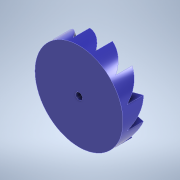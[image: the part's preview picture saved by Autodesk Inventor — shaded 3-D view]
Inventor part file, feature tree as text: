
AUTODESK INVENTOR PART (.ipt)
format: ipt  version: 2021 (Build 250183000, 183)  size: 309,760 bytes
history: native  units: in
note: dims shown in document units (in); Inventor stores cm internally (conversion verified against a paired STEP export)
features: other x3, extrude x2, sketch x2, fillet x1, plane x1
ambient origin geometry x8: Origin, YZ Plane, XZ Plane, XY Plane, X Axis, Y Axis, Z Axis, Center Point
bodies: Solid1 (feature_tree)
feature tree (9):
  other  "mergedprototype.iam"
  other  "prototypeDown.ipt:1"
  other  "cylinder.ipt:1"
  extrude  "Extrusion1"  Depth=0.3937in
  fillet  "Fillet1"  Radius=1.2in
  extrude  "Extrusion2"  Depth=0.0312in
  plane  "Work Plane1"
  sketch  "Sketch1"  dims[d0=0.3937in d1=1.6in d2=1.2in]
  sketch  "Sketch2"  dims[d3=0.35in d4=0.0in d5=0.0312in d6=0.315in d7=0.0in d8=0.0in]
